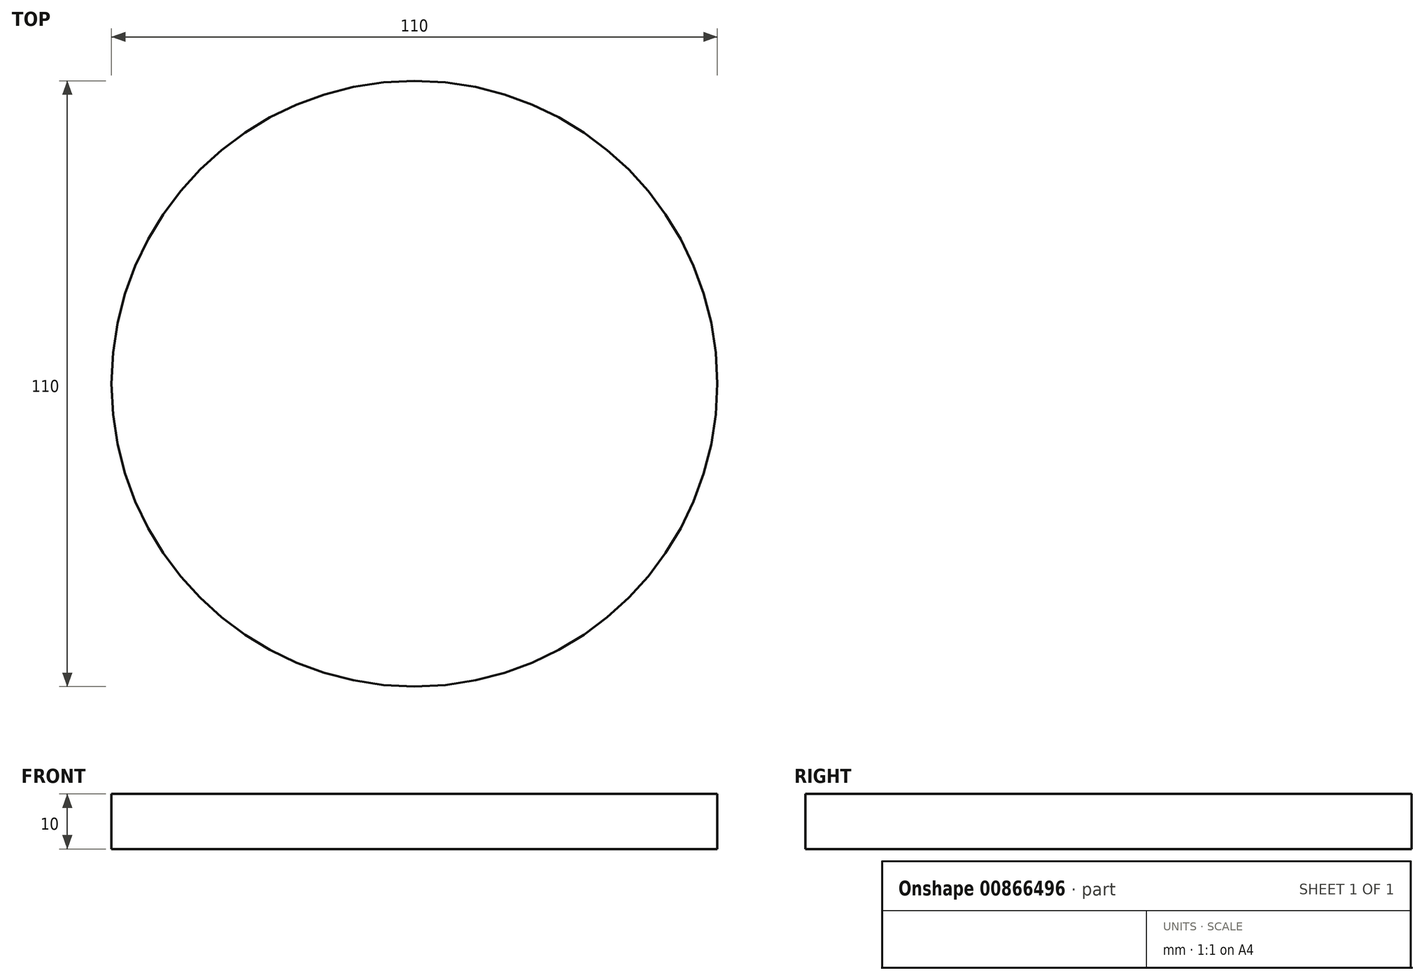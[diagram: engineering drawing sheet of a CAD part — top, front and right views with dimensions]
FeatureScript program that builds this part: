
annotation { "Feature Type Name" : "Feature", "Feature Type Description" : "" }
export const myFeature = defineFeature(function(context is Context, id is Id, definition is map)
    precondition{}
    {
        {
            var Q0;
            Q0=qCreatedBy(makeId("Top.planeOp"),FACE);
            var sketch = newSketch(context, id + "F0", { "sketchPlane" : qUnion([Q0])});
            skCircle(sketch, "E0", {"center": v(0, 0) * mm, "radius": 55 * mm});
            skSolve(sketch);
        }
        {
            var Q0;
            Q0 = qSketchRegion(id + "F0", true);
            extrude(context, id + "F1", {"entities" : qUnion([Q0]), "depth" : 10 * mm, "offsetDistance" : 25 * mm});
        }
    });
